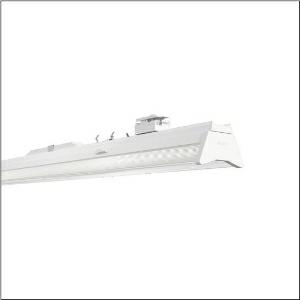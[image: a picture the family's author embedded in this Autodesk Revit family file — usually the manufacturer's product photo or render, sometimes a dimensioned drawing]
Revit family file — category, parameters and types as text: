
# Revit family: licross_r__21_performance_mo_52tm16dn445g_a9c4
name_source: partatom
category: Lighting Fixtures
units: mm (PartAtom-declared; Revit-internal decimal feet)

## family parameters
Cut with Voids When Loaded = No
Host = Face
Light Source = No
Part Type = Normal
Room Calculation Point = No
Round Connector Dimension = Use Diameter
Shared = No

## types (1)
- --- (1 x LED, 4500 lm, 24.9 W, 4000K)
    Apparent Load = 25 VA
    CIE Flux Codes = 66 88 96 79 100
    Color Rendering = 80
    Color Temperature = 4000K
    Default Elevation = 1800 mm
    Description = Licross® 21 Performance MO, luminaire insert, of sheet steel, galvanised, coil coated, white, length: 1.500mm, width: 120mm, height: 123mm, LED rated luminous flux: 4.500lm, light colour: 840, control gear: DALI 2, with plug, 5-pole, with phase selection, mains connection: 220..240V, AC, 50/60Hz, rated input power: 25W, internal wiring halogen-free, primary light control with lens, of plastic, primary optical cover: cover, of PMMA, CAT 2 (L<= 3000cd/m²), light emission: direct/indirect distribution, primary light characteristic: symmetric, protection rating (complete): IP40, insulation class (complete): insulation class I (protective earthing), certification: CE, ENEC, UKCA, protection symbol: D if used in an environment without relevant dust loads with corresponding accessories, impact resistance: IK06, permissible ambient temperature for indoor applications: -25..+50°C, corresponds to IFS (International Featured Standards) requirements for safety and quality in the food industry, reducing of maximum allowable ambient temperature of 5°C with ceiling mounting, LABS conformity tested according to VDMA 24364:2018-05, packaging unit: 1 piece
    Height = 114 mm
    Lamp = 1 x LED
    Lamp Light Flux = 4500 lm
    Lamp Power = 24.9 W
    Lamp count = 1
    Length = 1500 mm
    Luminous efficacy = 181 lm/W
    Manufacturer = Siteco
    ModVariant = No
    Model = 52TM16DN445G
    Mounting Place = Ceiling
    Mounting Type = Pendant
    Number of Poles = 1
    OnlyDefault = Yes
    Power Factor = 1
    Product Name = Licross® 21 Performance MO
    Product group = luminaire insert | ceiling pendant
    ProductGroupID = 902
    Protection Class = Protection class I
    Protection Degree = IP 40
    RLX_Detail_Level = 1
    RLX_Emergency_Light_Flux = 0 lm
    RLX_Emergency_Type = 0
    RLX_Emergency_Type_DB = No
    RlxData = <blob elided: 33553 chars, md5=fb5a80e0>
    Socket = socket
    Standby Power = 0 W
    System Light Flux = 4500 lm
    System Power = 25 W
    Type Comments = factory setting: luminous flux: 100 % | dim-lin: 254 | 165 mA
    Type Image = l_1256138.jpg
    URL = http://relux.com
    VarID = @adj_069911
    Voltage = 0 V
    Weight = 0.00 kg
    Width = 120 mm

## geometry (parser evidence)
native form markers: Blend x4, Sweep x12
no freeform markers — native parametric forms only
